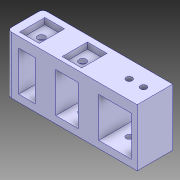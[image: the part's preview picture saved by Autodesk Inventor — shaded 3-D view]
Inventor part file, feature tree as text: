
AUTODESK INVENTOR PART (.ipt)
format: ipt  version: 2018 (Build 220112000, 112)  size: 195,584 bytes
history: native  units: mm
features: other x6, extrude x2, sketch x2, fillet x1
ambient origin geometry x8: Origin, YZ Plane, XZ Plane, XY Plane, X Axis, Y Axis, Z Axis, Center Point
bodies: Body1 (feature_tree)
feature tree (11):
  other  "Sólido1"
  extrude  "Extrusión1"  Depth=12.3mm
  other  "Edición directa1"
  extrude  "Extrusión2"  Depth=10.0mm TaperAngle=0.0deg
  other  "Edición directa2"
  fillet  "Empalme1"  Radius=1.0mm
  sketch  "Boceto1"  dims[d0=9.6mm d1=12.3mm]
  sketch  "Boceto2"  dims[d2=9.6mm d3=10.0mm d4=0.0mm d5=0.0mm d6=0.0mm d7=1.0mm d8=5.0mm d9=5.0mm d10=5.0mm d11=5.0mm d12=10.0mm d13=0.0mm d14=0.0mm d15=0.0mm d16=4.935mm d17=2.0mm]
  other  "PartBody"
  other  "Desplazar1"
  other  "Desplazar2"
